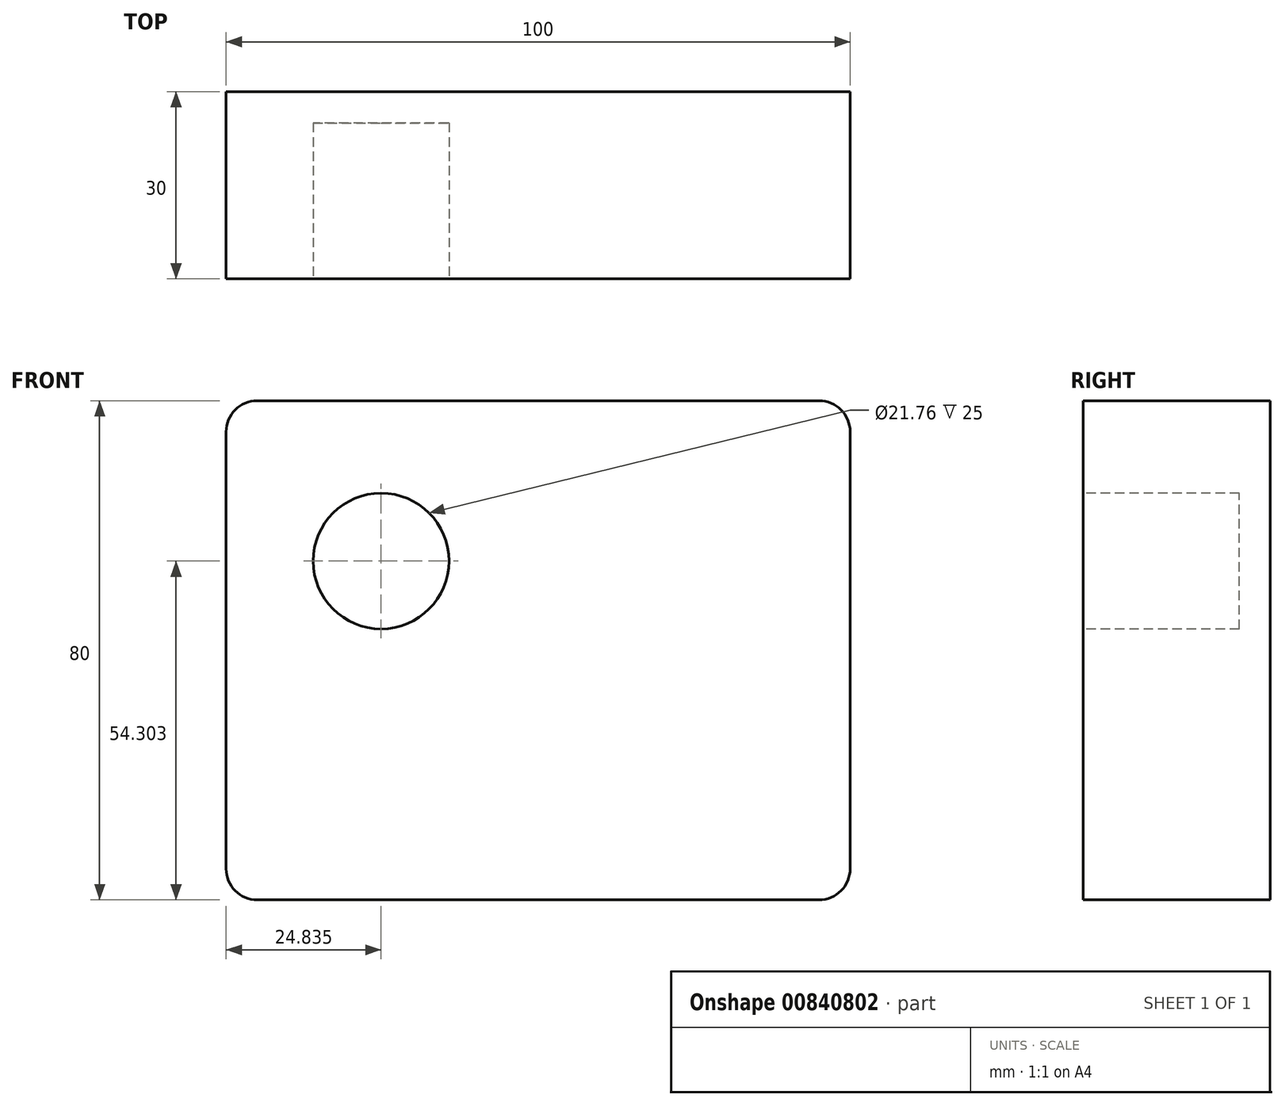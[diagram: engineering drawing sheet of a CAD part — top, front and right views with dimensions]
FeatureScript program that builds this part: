
annotation { "Feature Type Name" : "Feature", "Feature Type Description" : "" }
export const myFeature = defineFeature(function(context is Context, id is Id, definition is map)
    precondition{}
    {
        {
            var Q0;
            Q0=qCreatedBy(makeId("Front.planeOp"),FACE);
            var sketch = newSketch(context, id + "F0", { "sketchPlane" : qUnion([Q0])});
            skLineSegment(sketch, "E0.bottom", {"start": v(0, 0) * mm, "end": v(100, 0) * mm});
            skLineSegment(sketch, "E0.top", {"start": v(0, 80) * mm, "end": v(100, 80) * mm});
            skLineSegment(sketch, "E0.left", {"start": v(0, 0) * mm, "end": v(0, 80) * mm});
            skLineSegment(sketch, "E0.right", {"start": v(100, 0) * mm, "end": v(100, 80) * mm});
            skSolve(sketch);
        }
        {
            var Q0;
            Q0 = qSketchRegion(id + "F0", true);
            extrude(context, id + "F1", {"entities" : qUnion([Q0]), "depth" : 30 * mm, "offsetDistance" : 25 * mm});
        }
        {
            var Q0;
            Q0=makeQuery(id+"F1.opExtrude","CAP_FACE",FACE,{"disambiguationData":[OSD([sQuery(id+"F0.wireOp",EDGE,"E0.bottom"),sQuery(id+"F0.wireOp",EDGE,"E0.top"),sQuery(id+"F0.wireOp",EDGE,"E0.left"),sQuery(id+"F0.wireOp",EDGE,"E0.right")])],"isStart":false});
            var sketch = newSketch(context, id + "F2", { "sketchPlane" : qUnion([Q0])});
            skCircle(sketch, "E1", {"center": v(24.84, 54.3) * mm, "radius": 10.88 * mm});
            skSolve(sketch);
        }
        {
            var Q0;
            Q0 = qSketchRegion(id + "F2", true);
            extrude(context, id + "F3", {"entities" : qUnion([Q0]), "operationType" : NewBodyOperationType.REMOVE, "oppositeDirection" : true, "depth" : 25 * mm, "offsetDistance" : 25 * mm});
        }
        {
            var Q0;
            Q0=makeQuery(id+"F1.opExtrude","SWEPT_EDGE",EDGE,{"disambiguationData":[OSD([sQuery(id+"F0.wireOp",EDGE,"E0.top"),sQuery(id+"F0.wireOp",EDGE,"E0.left")])]});
            var Q1;
            Q1=makeQuery(id+"F1.opExtrude","SWEPT_EDGE",EDGE,{"disambiguationData":[OSD([sQuery(id+"F0.wireOp",EDGE,"E0.top"),sQuery(id+"F0.wireOp",EDGE,"E0.right")])]});
            var Q2;
            Q2=makeQuery(id+"F1.opExtrude","SWEPT_EDGE",EDGE,{"disambiguationData":[OSD([sQuery(id+"F0.wireOp",EDGE,"E0.bottom"),sQuery(id+"F0.wireOp",EDGE,"E0.right")])]});
            var Q3;
            Q3=makeQuery(id+"F1.opExtrude","SWEPT_EDGE",EDGE,{"disambiguationData":[OSD([sQuery(id+"F0.wireOp",EDGE,"E0.bottom"),sQuery(id+"F0.wireOp",EDGE,"E0.left")])]});
            fillet(context, id + "F4", {"entities" : qUnion([Q0, Q1, Q2, Q3]), "radius" : 5 * mm, "tangentPropagation" : true, "allowEdgeOverflow" : false});
        }
    });
